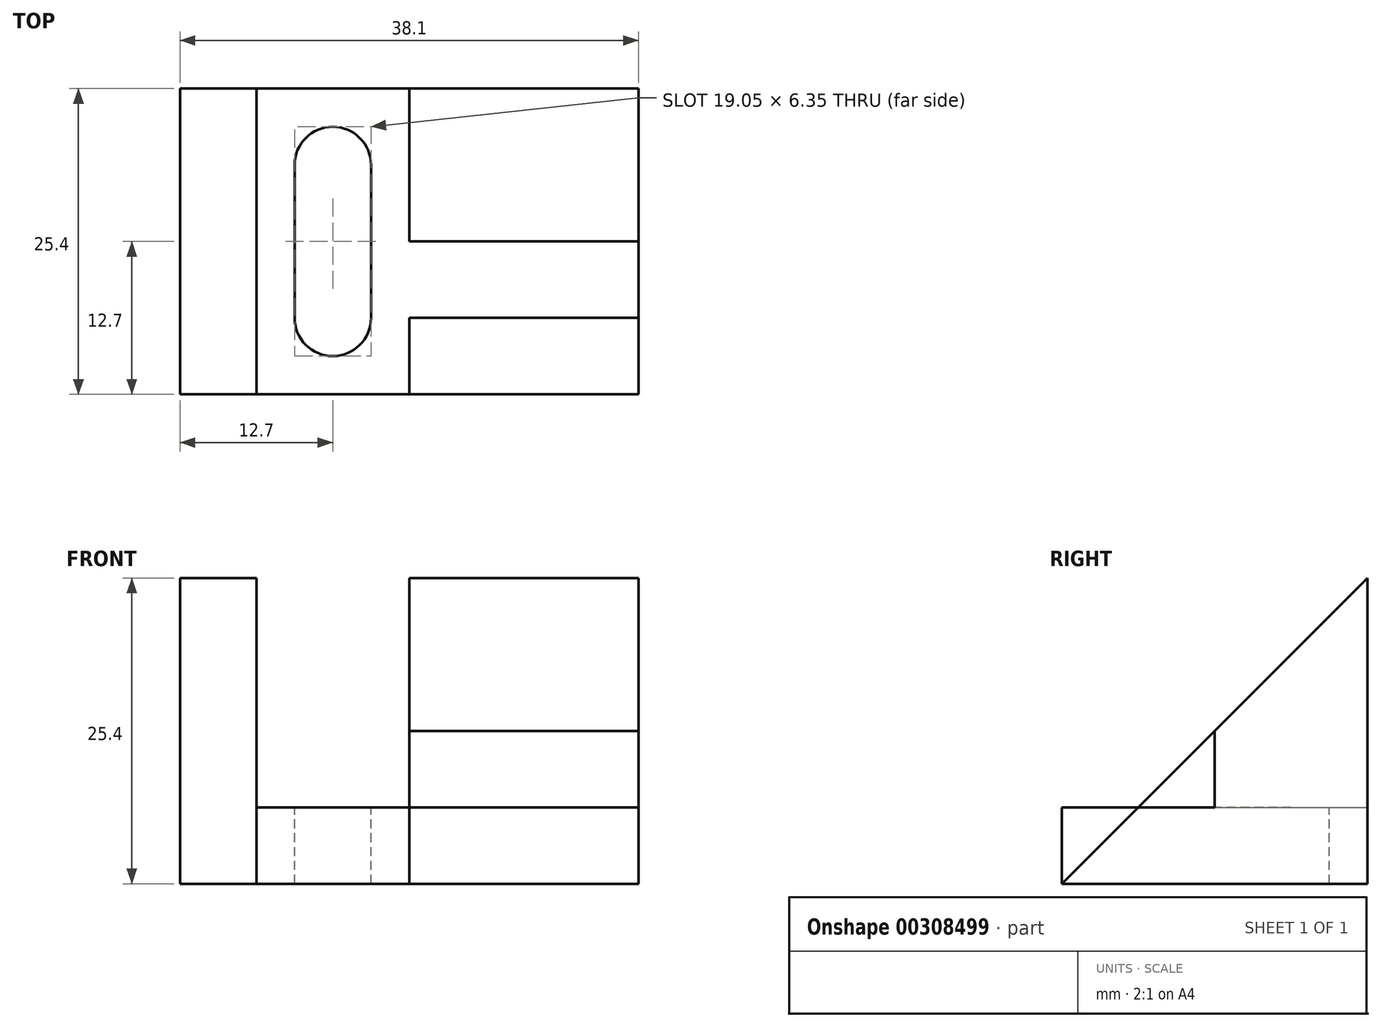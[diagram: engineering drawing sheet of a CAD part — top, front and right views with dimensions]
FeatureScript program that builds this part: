
annotation { "Feature Type Name" : "Feature", "Feature Type Description" : "" }
export const myFeature = defineFeature(function(context is Context, id is Id, definition is map)
    precondition{}
    {
        {
            var Q0;
            Q0=qCreatedBy(makeId("Right.planeOp"),FACE);
            var sketch = newSketch(context, id + "F0", { "sketchPlane" : qUnion([Q0])});
            skLineSegment(sketch, "E0", {"start": v(0, 0) * mm, "end": v(0, 25.4) * mm});
            skLineSegment(sketch, "E1", {"start": v(0, 25.4) * mm, "end": v(-25.4, 0) * mm});
            skLineSegment(sketch, "E2", {"start": v(-25.4, 0) * mm, "end": v(0, 0) * mm});
            skLineSegment(sketch, "E3", {"start": v(-12.7, 0) * mm, "end": v(-12.7, 12.7) * mm});
            skLineSegment(sketch, "E4", {"start": v(-25.4, 0) * mm, "end": v(-25.4, 6.35) * mm});
            skLineSegment(sketch, "E5", {"start": v(-25.4, 6.35) * mm, "end": v(-12.7, 6.35) * mm});
            skLineSegment(sketch, "E6", {"start": v(-12.7, 6.35) * mm, "end": v(-12.7, 0) * mm});
            skSolve(sketch);
        }
        {
            var Q0;
            Q0 = qSketchRegion(id + "F0", true);
            extrude(context, id + "F1", {"entities" : qUnion([Q0]), "endBound" : BoundingType.SYMMETRIC, "oppositeDirection" : true, "depth" : 38.1 * mm});
        }
        {
            var Q0;
            {var subQ3=sQuery(id+"F0.wireOp",EDGE,"E3");Q0=makeQuery(id+"F0.imprint","IMPRINT",FACE,{"disambiguationData":[TD([[makeQuery(id+"F0.imprint","IMPRINT",EDGE,{"derivedFrom":subQ3}),1.0]])]});}
            var Q1;
            {var subQ0=sQuery(id+"F0.wireOp",EDGE,"E4");Q1=makeQuery(id+"F0.imprint","IMPRINT",FACE,{"disambiguationData":[TD([[makeQuery(id+"F0.imprint","IMPRINT",EDGE,{"derivedFrom":subQ0}),-1.0]])]});}
            var Q2;
            {var subQ5=sQuery(id+"F0.wireOp",EDGE,"E6");Q2=makeQuery(id+"F0.imprint","IMPRINT",FACE,{"disambiguationData":[TD([[makeQuery(id+"F0.imprint","IMPRINT",EDGE,{"derivedFrom":subQ5}),-1.0]])]});}
            extrude(context, id + "F2", {"entities" : qUnion([Q0, Q1, Q2]), "operationType" : NewBodyOperationType.REMOVE, "depth" : 19.05 * mm});
        }
        {
            var Q0;
            Q0=makeQuery(id+"F1.opExtrude","SWEPT_FACE",FACE,{"disambiguationData":[OSD([sQuery(id+"F0.wireOp",EDGE,"E0")])]});
            var sketch = newSketch(context, id + "F3", { "sketchPlane" : qUnion([Q0])});
            skLineSegment(sketch, "E7", {"start": v(0, 6.35) * mm, "end": v(0, 25.4) * mm});
            skLineSegment(sketch, "E8", {"start": v(0, 25.4) * mm, "end": v(12.7, 25.4) * mm});
            skLineSegment(sketch, "E9", {"start": v(12.7, 25.4) * mm, "end": v(12.7, 6.35) * mm});
            skLineSegment(sketch, "E10", {"start": v(12.7, 6.35) * mm, "end": v(0, 6.35) * mm});
            skSolve(sketch);
        }
        {
            var Q0;
            Q0=makeQuery(id+"F3.imprint","IMPRINT",FACE,{"disambiguationData":[TD([[makeQuery(id+"F3.imprint","IMPRINT",EDGE,{"derivedFrom":sQuery(id+"F3.wireOp",EDGE,"E7")}),-1.0]])]});
            extrude(context, id + "F4", {"entities" : qUnion([Q0]), "operationType" : NewBodyOperationType.REMOVE, "oppositeDirection" : true, "depth" : 25.4 * mm});
        }
        {
            var Q0;
            Q0=makeQuery(id+"F1.opExtrude","CAP_FACE",FACE,{"disambiguationData":[OSD([sQuery(id+"F0.wireOp",EDGE,"E0"),sQuery(id+"F0.wireOp",EDGE,"E1"),sQuery(id+"F0.wireOp",EDGE,"E2"),sQuery(id+"F0.wireOp",EDGE,"E4"),sQuery(id+"F0.wireOp",EDGE,"E5")])],"isStart":false});
            var sketch = newSketch(context, id + "F5", { "sketchPlane" : qUnion([Q0])});
            skLineSegment(sketch, "E11", {"start": v(19.05, 6.35) * mm, "end": v(25.4, 0) * mm});
            skLineSegment(sketch, "E12", {"start": v(19.05, 6.35) * mm, "end": v(25.4, 6.35) * mm});
            skLineSegment(sketch, "E13", {"start": v(25.4, 6.35) * mm, "end": v(25.4, 0) * mm});
            skSolve(sketch);
        }
        {
            var Q0;
            Q0=makeQuery(id+"F5.imprint","IMPRINT",FACE,{"disambiguationData":[TD([[makeQuery(id+"F5.imprint","IMPRINT",EDGE,{"derivedFrom":sQuery(id+"F5.wireOp",EDGE,"E11")}),1.0]])]});
            extrude(context, id + "F6", {"entities" : qUnion([Q0]), "operationType" : NewBodyOperationType.REMOVE, "oppositeDirection" : true, "depth" : 6.35 * mm});
        }
        {
            var Q0;
            Q0=makeQuery(id+"F4.boolean.opBoolean","MERGE",FACE,{"derivedFrom":[makeQuery(id+"F1.opExtrude","SWEPT_FACE",FACE,{"disambiguationData":[OSD([sQuery(id+"F0.wireOp",EDGE,"E5")])]}),makeQuery(id+"F4.opExtrude","SWEPT_FACE",FACE,{"disambiguationData":[OSD([sQuery(id+"F3.wireOp",EDGE,"E10")])]})]});
            var sketch = newSketch(context, id + "F7", { "sketchPlane" : qUnion([Q0])});
            skLineSegment(sketch, "E14", {"start": v(-6.35, 0) * mm, "end": v(-6.35, -25.4) * mm, "construction": true});
            skLineSegment(sketch, "E15", {"start": v(-12.7, -6.35) * mm, "end": v(0, -6.35) * mm, "construction": true});
            skLineSegment(sketch, "E16", {"start": v(0, -19.05) * mm, "end": v(-12.7, -19.05) * mm, "construction": true});
            skLineSegment(sketch, "E17", {"start": v(-9.52, -6.35) * mm, "end": v(-9.52, -19.05) * mm});
            skLineSegment(sketch, "E18", {"start": v(-3.17, -6.35) * mm, "end": v(-3.17, -19.05) * mm});
            skArc(sketch, "E19", {"start": v(-3.17, -6.35) * mm, "mid": v(-6.35, -3.17) * mm, "end": v(-9.52, -6.35) * mm});
            skArc(sketch, "E20", {"start": v(-9.52, -19.05) * mm, "mid": v(-6.35, -22.22) * mm, "end": v(-3.17, -19.05) * mm});
            skSolve(sketch);
        }
        {
            var Q0;
            Q0=makeQuery(id+"F7.imprint","IMPRINT",FACE,{"disambiguationData":[TD([[makeQuery(id+"F7.imprint","IMPRINT",EDGE,{"derivedFrom":sQuery(id+"F7.wireOp",EDGE,"E17")}),1.0]])]});
            var Q1;
            Q1=makeQuery(id+"F1.opExtrude","SWEPT_FACE",FACE,{"disambiguationData":[OSD([sQuery(id+"F0.wireOp",EDGE,"E2")])]});
            extrude(context, id + "F8", {"entities" : qUnion([Q0]), "operationType" : NewBodyOperationType.REMOVE, "endBound" : BoundingType.UP_TO_SURFACE, "oppositeDirection" : true, "endBoundEntityFace" : qUnion([Q1]), "depth" : 25.4 * mm});
        }
    });
